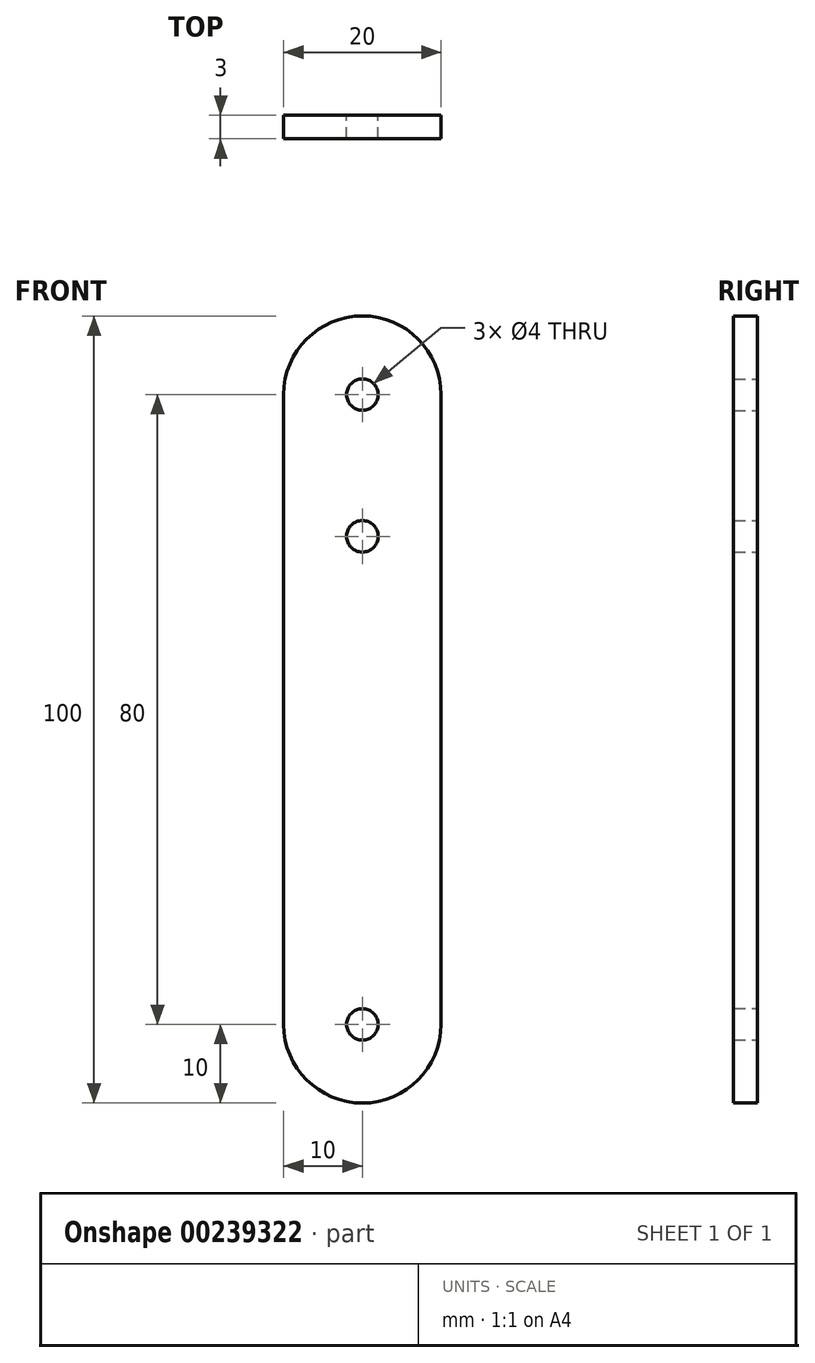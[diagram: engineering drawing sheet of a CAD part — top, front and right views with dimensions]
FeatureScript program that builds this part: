
annotation { "Feature Type Name" : "Feature", "Feature Type Description" : "" }
export const myFeature = defineFeature(function(context is Context, id is Id, definition is map)
    precondition{}
    {
        {
            var Q0;
            Q0=qCreatedBy(makeId("Front.planeOp"),FACE);
            var sketch = newSketch(context, id + "F0", { "sketchPlane" : qUnion([Q0])});
            skLineSegment(sketch, "E0.bottom", {"start": v(10, -40) * mm, "end": v(-10, -40) * mm, "construction": true});
            skLineSegment(sketch, "E0.top", {"start": v(10, 40) * mm, "end": v(-10, 40) * mm, "construction": true});
            skLineSegment(sketch, "E0.left", {"start": v(10, -40) * mm, "end": v(10, 40) * mm});
            skLineSegment(sketch, "E0.right", {"start": v(-10, -40) * mm, "end": v(-10, 40) * mm});
            skPoint(sketch, "E0.middle", {"position": v(0, 0) * mm});
            skArc(sketch, "E1", {"start": v(10, 40) * mm, "mid": v(0, 50) * mm, "end": v(-10, 40) * mm});
            skArc(sketch, "E2", {"start": v(-10, -40) * mm, "mid": v(0, -50) * mm, "end": v(10, -40) * mm});
            skCircle(sketch, "E3", {"center": v(0, 40) * mm, "radius": 2 * mm});
            skCircle(sketch, "E4", {"center": v(0, -40) * mm, "radius": 2 * mm});
            skCircle(sketch, "E5", {"center": v(0, 22) * mm, "radius": 2 * mm});
            skSolve(sketch);
        }
        {
            var Q0;
            Q0=makeQuery(id+"F0.imprint","IMPRINT",FACE,{"disambiguationData":[TD([[makeQuery(id+"F0.imprint","IMPRINT",EDGE,{"derivedFrom":sQuery(id+"F0.wireOp",EDGE,"E0.left")}),1.0]])]});
            extrude(context, id + "F1", {"entities" : qUnion([Q0]), "depth" : 3 * mm});
        }
    });
